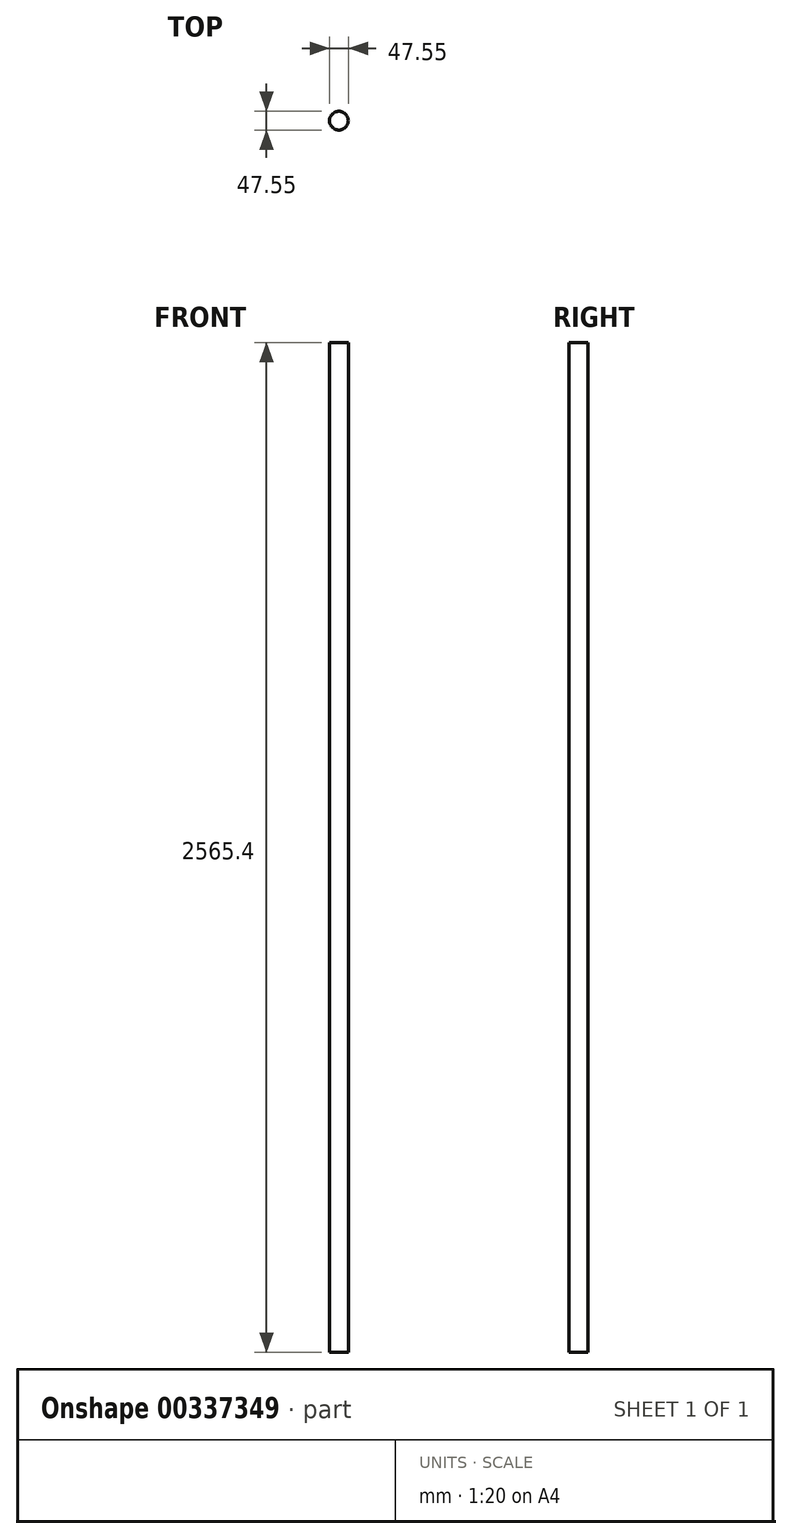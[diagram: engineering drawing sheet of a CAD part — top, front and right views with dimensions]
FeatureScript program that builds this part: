
annotation { "Feature Type Name" : "Feature", "Feature Type Description" : "" }
export const myFeature = defineFeature(function(context is Context, id is Id, definition is map)
    precondition{}
    {
        {
            var Q0;
            Q0=qCreatedBy(makeId("Top.planeOp"),FACE);
            var sketch = newSketch(context, id + "F0", { "sketchPlane" : qUnion([Q0])});
            skCircle(sketch, "E0", {"center": v(-5.5, 2.15) * mm, "radius": 23.77 * mm});
            skSolve(sketch);
        }
        {
            var Q0;
            Q0=makeQuery(id+"F0.imprint","IMPRINT",FACE,{"disambiguationData":[TD([[makeQuery(id+"F0.imprint","IMPRINT",EDGE,{"derivedFrom":sQuery(id+"F0.wireOp",EDGE,"E0")}),1.0]])]});
            extrude(context, id + "F1", {"entities" : qUnion([Q0]), "depth" : 25.4 * mm});
        }
        {
            var Q0;
            Q0=makeQuery(id+"F1.opExtrude","CAP_FACE",FACE,{"disambiguationData":[OSD([sQuery(id+"F0.wireOp",EDGE,"E0")])],"isStart":false});
            extrude(context, id + "F2", {"entities" : qUnion([Q0]), "operationType" : NewBodyOperationType.ADD, "depth" : 2540 * mm});
        }
    });
